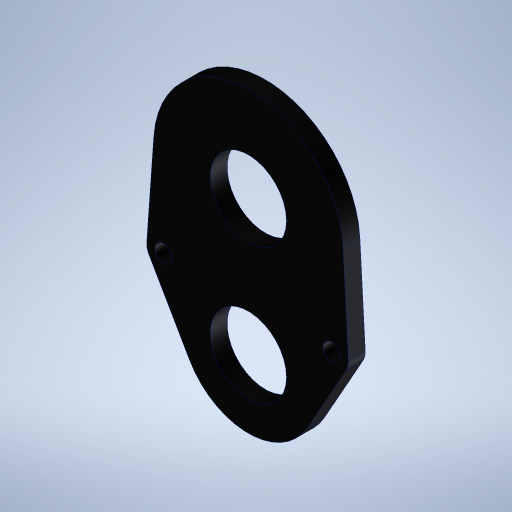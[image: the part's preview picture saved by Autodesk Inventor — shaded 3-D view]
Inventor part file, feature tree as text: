
AUTODESK INVENTOR PART (.ipt)
format: ipt  version: 2024 (Build 280153000, 153)  size: 272,896 bytes
history: native  units: in
note: dims shown in document units (in); Inventor stores cm internally (conversion verified against a paired STEP export)
features: extrude x1, sketch x1
ambient origin geometry x8: Origin, YZ Plane, XZ Plane, XY Plane, X Axis, Y Axis, Z Axis, Center Point
bodies: Body1 (feature_tree)
feature tree (2):
  extrude  "Extrusion2"  Depth=0.25in
  sketch  "Sketch1"  dims[d0=1.125in d1=1.6in d2=2.4in d3=1.125in d4=0.2in d5=2.8in d6=0.2in d9=0.5in d10=0.125in d11=0.257in d12=0.257in d13=0.25in d14=0.0in]
